# Revit family: Haworth_ASeries_Credenza_2High
name_source: partatom
category: Furniture Systems
revit_build: Autodesk Revit 2018 (Build: 20170223_1515(x64)
units: mm (PartAtom-declared; Revit-internal decimal feet)

## family parameters
Always vertical = Yes
Cut with Voids When Loaded = No
OmniClass Number = 23.40.70.14.64.21
OmniClass Title = Systems Furniture
Part Type = Normal
Room Calculation Point = No
Round Connector Dimension = Use Diameter
Shared = No
Work Plane-Based = No

## types (6) — shared parameters
Actual Depth = 14 5/8"
Actual Height = 26 1/2"
Assembly Code = E2020200
Base Height = 2 1/2"
Classic Pull = Yes
Crescent Pull = No
Custom Size = No
Description = Haworth - ASeries Credenza - 2-High
Door Height = 17 3/16"
Door Offset = 2"
Door Width = 11 15/16"
Drawer Height = 6"
Drawer Width = 24"
Ellipse Pull = No
End Shelf Height = 12 3/4"
Front Finish = Haworth _ Laminate _ Linen H-WL
Full Back = Yes
J Pull = No
Linear Pull = No
Manufacturer = Haworth
Max. Height = 26 1/2"
Max. Width = 72"
Metal Offset = 1/16"
Min. Height = 26 1/2"
Min. Width = 48"
Min/Max Widths = 48-72 in.
Model = GCWN
Panel Center Offset = 12 1/8"
Panel Thickness = 1 1/4"
Pull Finish = Haworth _ Metal _ Brushed Aluminum
Radius Pull = No
Revision Number = 2
Shelf Finish = Haworth _ Laminate _ Linen H-WL
Size = Verify Final Dim. w/ Haworth
Standard Base = Yes
Storage Back = No
Sustainability Info = https://www.haworth.com
Taper Pull = No
Toe Kick Base = No
Toe Kick Height = 1 3/4"
Top Finish = Haworth _ Laminate _ Linen H-WL
URL = www.haworth.com
URL - Product = https://www.haworth.com
Warranty = http://www.haworth.com

## per-type parameters (varying)
| type | Actual Width | Door Center | Drawer and Doors | Middle Shelf Height | Open | Right Panel | Right Shelf Length | Shelf Offset | Width |
| 72w - Drawer and Doors | 72" | 36" | Yes | 16 3/4" | No | Yes | 23 7/8" | 3/4" | 72" |
| 72w - Open | 72" | 36" | No | 12 3/4" | Yes | Yes | 23 7/8" | 3/4" | 72" |
| 60w - Drawer and Doors | 60" | 30" | Yes | 16 3/4" | No | Yes | 17 7/8" | 3/4" | 60" |
| 60w - Open | 60" | 30" | No | 12 3/4" | Yes | Yes | 17 7/8" | 3/4" | 60" |
| 48w - Drawer and Doors | 48" | 13 3/8" | Yes | 16 3/4" | No | No | 11 7/8" | 1/16" | 48" |
| 48w - Open | 48" | 13 3/8" | No | 12 3/4" | Yes | No | 11 7/8" | 1/16" | 48" |

## geometry (parser evidence)
native form markers: Sweep x11
no freeform markers — native parametric forms only
